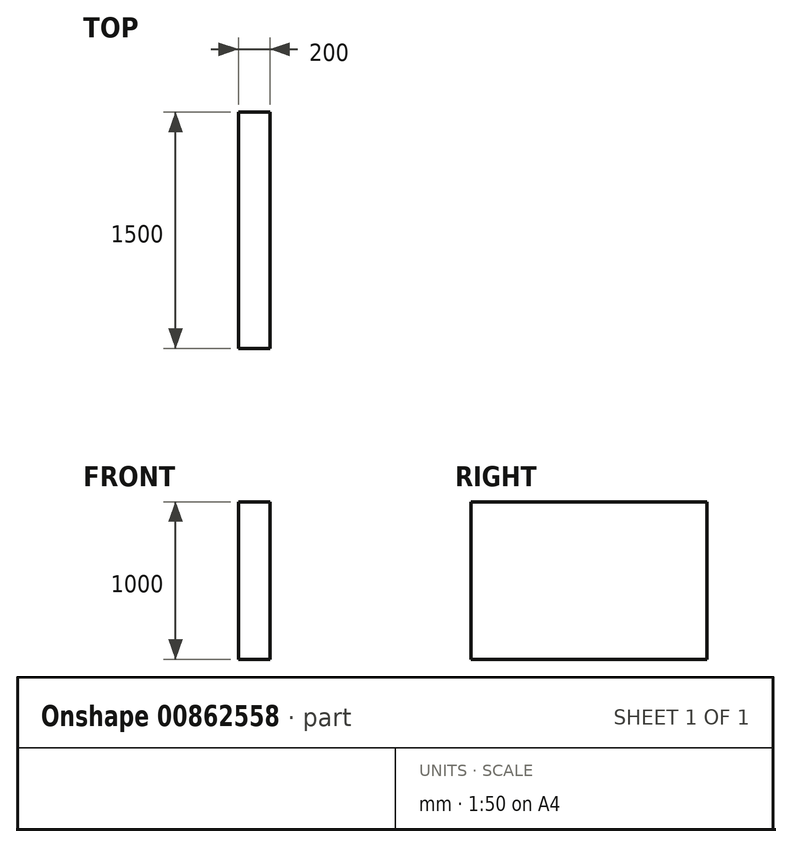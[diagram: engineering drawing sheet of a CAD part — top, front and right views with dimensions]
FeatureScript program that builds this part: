
annotation { "Feature Type Name" : "Feature", "Feature Type Description" : "" }
export const myFeature = defineFeature(function(context is Context, id is Id, definition is map)
    precondition{}
    {
        {
            var Q0;
            Q0=qCreatedBy(makeId("Front.planeOp"),FACE);
            var sketch = newSketch(context, id + "F0", { "sketchPlane" : qUnion([Q0])});
            skLineSegment(sketch, "E0.bottom", {"start": v(-200, 1000) * mm, "end": v(0, 1000) * mm});
            skLineSegment(sketch, "E0.top", {"start": v(-200, 0) * mm, "end": v(0, 0) * mm});
            skLineSegment(sketch, "E0.left", {"start": v(-200, 1000) * mm, "end": v(-200, 0) * mm});
            skLineSegment(sketch, "E0.right", {"start": v(0, 1000) * mm, "end": v(0, 0) * mm});
            skSolve(sketch);
        }
        {
            var Q0;
            Q0=makeQuery(id+"F0.imprint","IMPRINT",FACE,{"disambiguationData":[TD([[makeQuery(id+"F0.imprint","IMPRINT",EDGE,{"derivedFrom":sQuery(id+"F0.wireOp",EDGE,"E0.bottom")}),-1.0]])]});
            extrude(context, id + "F1", {"entities" : qUnion([Q0]), "depth" : 1500 * mm, "offsetDistance" : 25 * mm});
        }
    });
